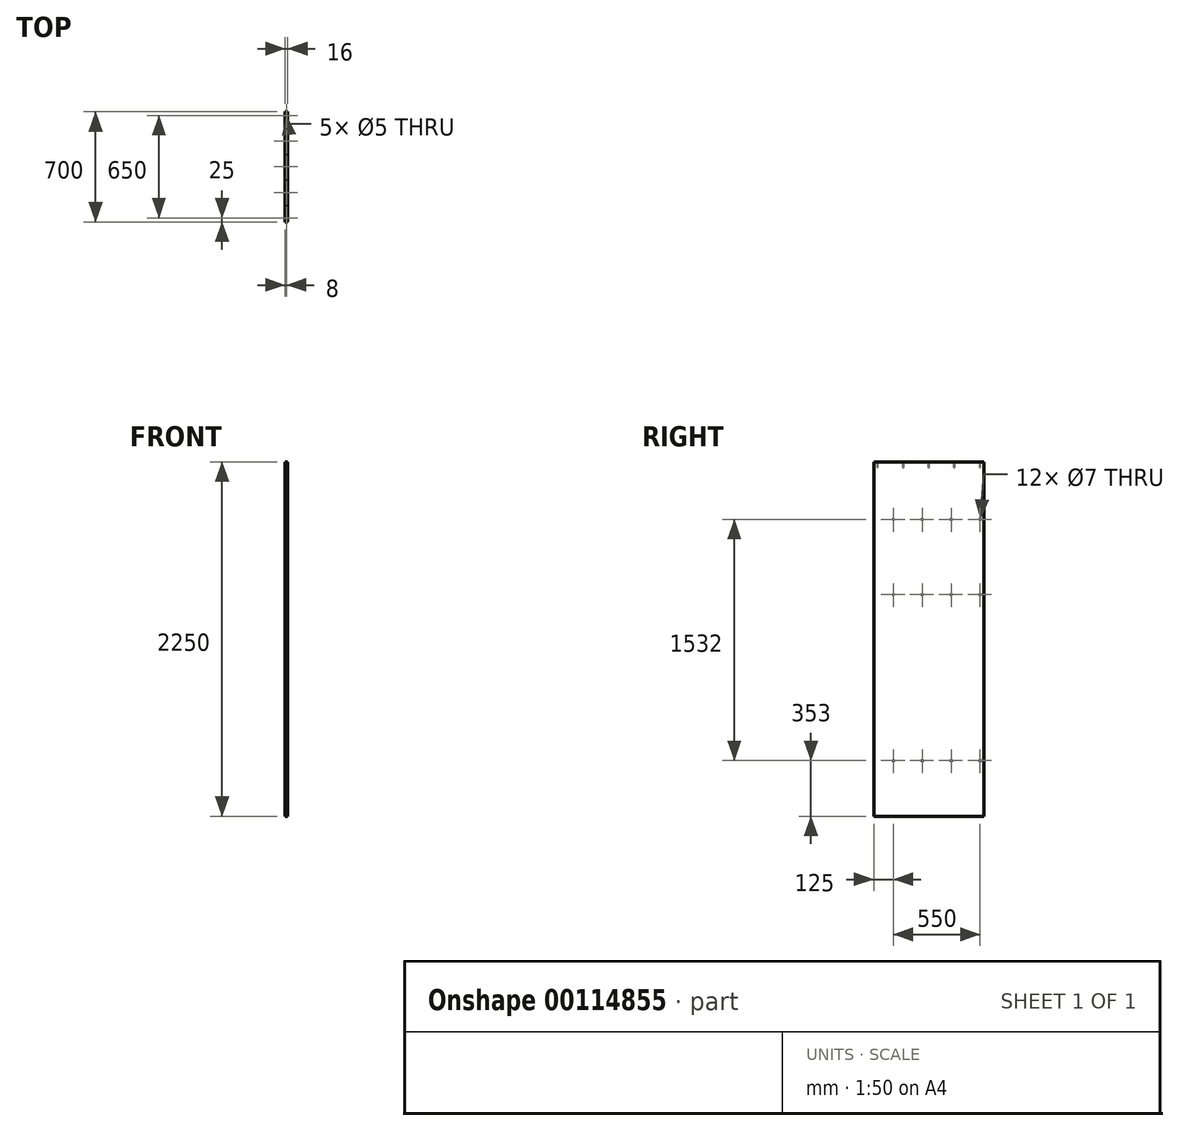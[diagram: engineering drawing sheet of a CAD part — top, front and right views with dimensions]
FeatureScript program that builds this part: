
annotation { "Feature Type Name" : "Feature", "Feature Type Description" : "" }
export const myFeature = defineFeature(function(context is Context, id is Id, definition is map)
    precondition{}
    {
        {
            var Q0;
            Q0=qCreatedBy(makeId("Right.planeOp"),FACE);
            var sketch = newSketch(context, id + "F0", { "sketchPlane" : qUnion([Q0])});
            skLineSegment(sketch, "E0.bottom", {"start": v(-350, -1125) * mm, "end": v(350, -1125) * mm});
            skLineSegment(sketch, "E0.top", {"start": v(-350, 1125) * mm, "end": v(350, 1125) * mm});
            skLineSegment(sketch, "E0.left", {"start": v(-350, -1125) * mm, "end": v(-350, 1125) * mm});
            skLineSegment(sketch, "E0.right", {"start": v(350, -1125) * mm, "end": v(350, 1125) * mm});
            skPoint(sketch, "E0.middle", {"position": v(0, 0) * mm});
            skSolve(sketch);
        }
        {
            var Q0;
            Q0=makeQuery(id+"F0.imprint","IMPRINT",FACE,{"disambiguationData":[TD([[makeQuery(id+"F0.imprint","IMPRINT",EDGE,{"derivedFrom":sQuery(id+"F0.wireOp",EDGE,"E0.bottom")}),1.0]])]});
            extrude(context, id + "F1", {"entities" : qUnion([Q0]), "endBound" : BoundingType.SYMMETRIC, "depth" : 16 * mm});
        }
        {
            var Q0;
            Q0=makeQuery(id+"F1.opExtrude","SWEPT_FACE",FACE,{"disambiguationData":[OSD([sQuery(id+"F0.wireOp",EDGE,"E0.top")])]});
            var sketch = newSketch(context, id + "F2", { "sketchPlane" : qUnion([Q0])});
            skPoint(sketch, "E1", {"position": v(0, 325) * mm});
            skPoint(sketch, "E2", {"position": v(0, 0) * mm});
            skPoint(sketch, "E3", {"position": v(0, -325) * mm});
            skPoint(sketch, "E4", {"position": v(0, 162.5) * mm});
            skPoint(sketch, "E5", {"position": v(0, -162.5) * mm});
            skSolve(sketch);
        }
        {
            var Q0;
            Q0=sQuery(id+"F2.wireOp",VERTEX,"E1");
            var Q1;
            Q1=sQuery(id+"F2.wireOp",VERTEX,"E4");
            var Q2;
            Q2=sQuery(id+"F2.wireOp",VERTEX,"E2");
            var Q3;
            Q3=sQuery(id+"F2.wireOp",VERTEX,"E5");
            var Q4;
            Q4=sQuery(id+"F2.wireOp",VERTEX,"E3");
            var Q5;
            Q5=makeQuery(id+"F1.opExtrude","SWEPT_BODY",BODY,{"disambiguationData":[OSD([sQuery(id+"F0.wireOp",EDGE,"E0.bottom"),sQuery(id+"F0.wireOp",EDGE,"E0.top"),sQuery(id+"F0.wireOp",EDGE,"E0.left"),sQuery(id+"F0.wireOp",EDGE,"E0.right")])]});
            hole(context, id + "F3", {"style" : HoleStyle.C_SINK, "endStyle" : HoleEndStyle.BLIND, "holeDiameter" : 5 * mm, "cSinkDiameter" : 7 * mm, "cSinkAngle" : 90 * degree, "holeDepth" : 35 * mm, "locations" : qUnion([Q0, Q1, Q2, Q3, Q4]), "scope" : qUnion([Q5])});
        }
        {
            var Q0;
            Q0=makeQuery(id+"F1.opExtrude","CAP_FACE",FACE,{"disambiguationData":[OSD([sQuery(id+"F0.wireOp",EDGE,"E0.bottom"),sQuery(id+"F0.wireOp",EDGE,"E0.top"),sQuery(id+"F0.wireOp",EDGE,"E0.left"),sQuery(id+"F0.wireOp",EDGE,"E0.right")])],"isStart":false});
            var sketch = newSketch(context, id + "F4", { "sketchPlane" : qUnion([Q0])});
            skPoint(sketch, "E6", {"position": v(325, 760) * mm});
            skPoint(sketch, "E7", {"position": v(-225, 760) * mm});
            skPoint(sketch, "E8", {"position": v(-42, 760) * mm});
            skPoint(sketch, "E9", {"position": v(142, 760) * mm});
            skPoint(sketch, "E10", {"position": v(325, 283) * mm});
            skPoint(sketch, "E11", {"position": v(142, 283) * mm});
            skPoint(sketch, "E12", {"position": v(-42, 283) * mm});
            skPoint(sketch, "E13", {"position": v(-225, 283) * mm});
            skPoint(sketch, "E14", {"position": v(325, -772) * mm});
            skPoint(sketch, "E15", {"position": v(142, -772) * mm});
            skPoint(sketch, "E16", {"position": v(-42, -772) * mm});
            skPoint(sketch, "E17", {"position": v(-225, -772) * mm});
            skSolve(sketch);
        }
        {
            var Q0;
            Q0=sQuery(id+"F4.wireOp",VERTEX,"E7");
            var Q1;
            Q1=sQuery(id+"F4.wireOp",VERTEX,"E8");
            var Q2;
            Q2=sQuery(id+"F4.wireOp",VERTEX,"E9");
            var Q3;
            Q3=sQuery(id+"F4.wireOp",VERTEX,"E6");
            var Q4;
            Q4=sQuery(id+"F4.wireOp",VERTEX,"E10");
            var Q5;
            Q5=sQuery(id+"F4.wireOp",VERTEX,"E11");
            var Q6;
            Q6=sQuery(id+"F4.wireOp",VERTEX,"E12");
            var Q7;
            Q7=sQuery(id+"F4.wireOp",VERTEX,"E13");
            var Q8;
            Q8=sQuery(id+"F4.wireOp",VERTEX,"E14");
            var Q9;
            Q9=sQuery(id+"F4.wireOp",VERTEX,"E15");
            var Q10;
            Q10=sQuery(id+"F4.wireOp",VERTEX,"E16");
            var Q11;
            Q11=sQuery(id+"F4.wireOp",VERTEX,"E17");
            var Q12;
            Q12=sQuery(id+"F4.wireOp",VERTEX,"758fd1a7-2a68-45cb-af47-8f84281089d1");
            var Q13;
            Q13=sQuery(id+"F4.wireOp",VERTEX,"c11fbbc5-98d4-4946-ba18-f858bd2d77d2");
            var Q14;
            Q14=sQuery(id+"F4.wireOp",VERTEX,"1c99786c-cdbc-4969-9910-d7f580889aa1");
            var Q15;
            Q15=sQuery(id+"F4.wireOp",VERTEX,"6cc2c78b-1742-4060-bfba-05517046d845");
            var Q16;
            Q16=sQuery(id+"F4.wireOp",VERTEX,"4babea10-f120-4ea1-ac61-84ff34ca3672");
            var Q17;
            Q17=sQuery(id+"F4.wireOp",VERTEX,"2b295c81-de4a-42fb-9eae-e8896de7ea3b");
            var Q18;
            Q18=makeQuery(id+"F1.opExtrude","SWEPT_BODY",BODY,{"disambiguationData":[OSD([sQuery(id+"F0.wireOp",EDGE,"E0.bottom"),sQuery(id+"F0.wireOp",EDGE,"E0.top"),sQuery(id+"F0.wireOp",EDGE,"E0.left"),sQuery(id+"F0.wireOp",EDGE,"E0.right")])]});
            hole(context, id + "F5", {"style" : HoleStyle.SIMPLE, "endStyle" : HoleEndStyle.THROUGH, "holeDiameter" : 7 * mm, "locations" : qUnion([Q0, Q1, Q2, Q3, Q4, Q5, Q6, Q7, Q8, Q9, Q10, Q11, Q12, Q13, Q14, Q15, Q16, Q17]), "scope" : qUnion([Q18]), "isTappedThrough" : true});
        }
    });
